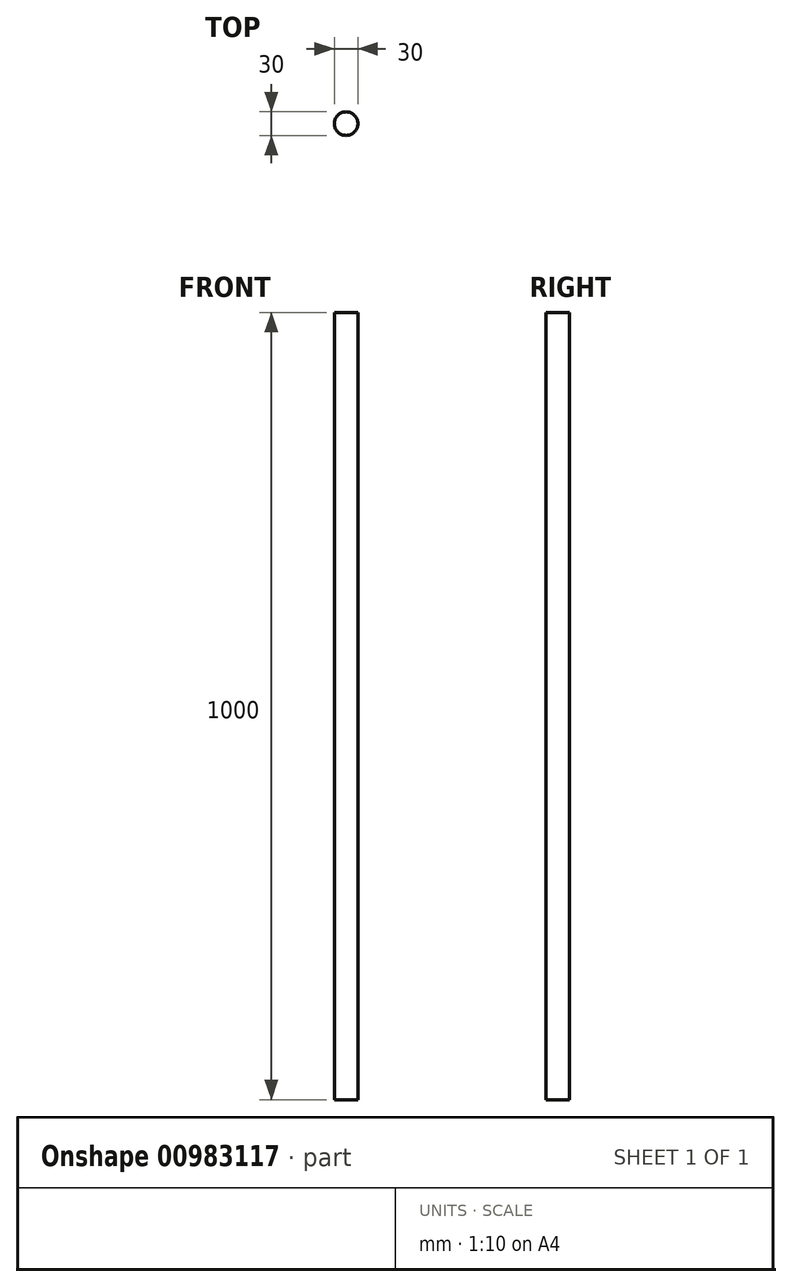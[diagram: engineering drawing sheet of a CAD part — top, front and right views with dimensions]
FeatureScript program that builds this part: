
annotation { "Feature Type Name" : "Feature", "Feature Type Description" : "" }
export const myFeature = defineFeature(function(context is Context, id is Id, definition is map)
    precondition{}
    {
        {
            var Q0;
            Q0=qCreatedBy(makeId("Top.planeOp"),FACE);
            var sketch = newSketch(context, id + "F0", { "sketchPlane" : qUnion([Q0])});
            skCircle(sketch, "E0", {"center": v(0, 0) * mm, "radius": 15 * mm});
            skSolve(sketch);
        }
        {
            var Q0;
            Q0 = qSketchRegion(id + "F0", true);
            extrude(context, id + "F1", {"entities" : qUnion([Q0]), "depth" : 1000 * mm, "offsetDistance" : 25 * mm});
        }
    });
